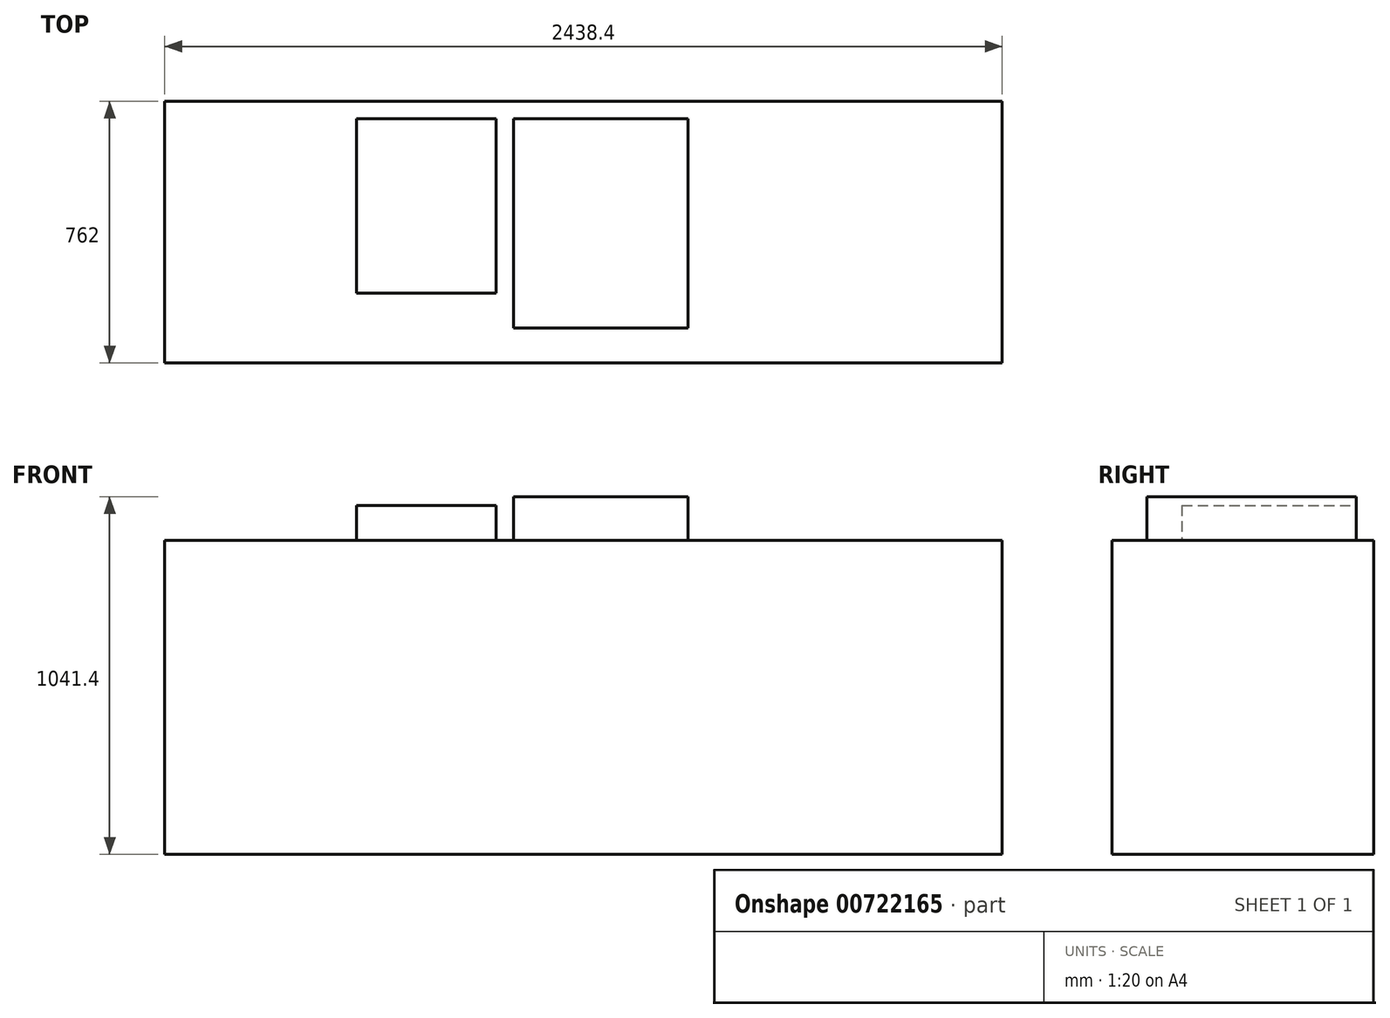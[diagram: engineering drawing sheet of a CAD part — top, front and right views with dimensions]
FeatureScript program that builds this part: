
annotation { "Feature Type Name" : "Feature", "Feature Type Description" : "" }
export const myFeature = defineFeature(function(context is Context, id is Id, definition is map)
    precondition{}
    {
        {
            var Q0;
            Q0=qCreatedBy(makeId("Top.planeOp"),FACE);
            var sketch = newSketch(context, id + "F0", { "sketchPlane" : qUnion([Q0])});
            skLineSegment(sketch, "E0.bottom", {"start": v(-1269.12, 762) * mm, "end": v(1169.28, 762) * mm});
            skLineSegment(sketch, "E0.top", {"start": v(-1269.12, 0) * mm, "end": v(1169.28, 0) * mm});
            skLineSegment(sketch, "E0.left", {"start": v(-1269.12, 762) * mm, "end": v(-1269.12, 0) * mm});
            skLineSegment(sketch, "E0.right", {"start": v(1169.28, 762) * mm, "end": v(1169.28, 0) * mm});
            skSolve(sketch);
        }
        {
            var Q0;
            Q0 = qSketchRegion(id + "F0", true);
            extrude(context, id + "F1", {"entities" : qUnion([Q0]), "depth" : 914.4 * mm, "offsetDistance" : 25.4 * mm});
        }
        {
            var Q0;
            Q0=makeQuery(id+"F1.opExtrude","CAP_FACE",FACE,{"disambiguationData":[OSD([sQuery(id+"F0.wireOp",EDGE,"E0.bottom"),sQuery(id+"F0.wireOp",EDGE,"E0.top"),sQuery(id+"F0.wireOp",EDGE,"E0.left"),sQuery(id+"F0.wireOp",EDGE,"E0.right")])],"isStart":false});
            var sketch = newSketch(context, id + "F2", { "sketchPlane" : qUnion([Q0])});
            skLineSegment(sketch, "E1", {"start": v(0, 711.2) * mm, "end": v(0, -341.85) * mm, "construction": true});
            skLineSegment(sketch, "E2.bottom", {"start": v(-254, 711.2) * mm, "end": v(254, 711.2) * mm});
            skLineSegment(sketch, "E2.top", {"start": v(-254, 101.6) * mm, "end": v(254, 101.6) * mm});
            skLineSegment(sketch, "E2.left", {"start": v(-254, 711.2) * mm, "end": v(-254, 101.6) * mm});
            skLineSegment(sketch, "E2.right", {"start": v(254, 711.2) * mm, "end": v(254, 101.6) * mm});
            skSolve(sketch);
        }
        {
            var Q0;
            Q0 = qSketchRegion(id + "F2", true);
            extrude(context, id + "F3", {"entities" : qUnion([Q0]), "depth" : 127 * mm, "offsetDistance" : 25.4 * mm});
        }
        {
            var Q0;
            Q0=makeQuery(id+"F1.opExtrude","CAP_FACE",FACE,{"disambiguationData":[OSD([sQuery(id+"F0.wireOp",EDGE,"E0.bottom"),sQuery(id+"F0.wireOp",EDGE,"E0.top"),sQuery(id+"F0.wireOp",EDGE,"E0.left"),sQuery(id+"F0.wireOp",EDGE,"E0.right")])],"isStart":false});
            var sketch = newSketch(context, id + "F4", { "sketchPlane" : qUnion([Q0])});
            skLineSegment(sketch, "E3.bottom", {"start": v(-304.8, 203.2) * mm, "end": v(-711.2, 203.2) * mm});
            skLineSegment(sketch, "E3.top", {"start": v(-304.8, 711.2) * mm, "end": v(-711.2, 711.2) * mm});
            skLineSegment(sketch, "E3.left", {"start": v(-304.8, 203.2) * mm, "end": v(-304.8, 711.2) * mm});
            skLineSegment(sketch, "E3.right", {"start": v(-711.2, 203.2) * mm, "end": v(-711.2, 711.2) * mm});
            skLineSegment(sketch, "E4.0", {"start": v(-1269.12, 762) * mm, "end": v(1169.28, 762) * mm, "construction": true});
            skSolve(sketch);
        }
        {
            var Q0;
            Q0 = qSketchRegion(id + "F4", true);
            extrude(context, id + "F5", {"entities" : qUnion([Q0]), "depth" : 101.6 * mm, "offsetDistance" : 25.4 * mm});
        }
    });
